# Revit family: Accessory-Teknion-EMWW_Thought_Board_Magnetic_Wood-R2016
name_source: partatom
category: Furniture
revit_build: Autodesk Revit 2018 (Build: 20190510_1515(x64)
units: mm (PartAtom-declared; Revit-internal decimal feet)

## family parameters
Always vertical = Yes
Cut with Voids When Loaded = No
OmniClass Number = 23.40.20.00
OmniClass Title = General Furniture and Specialties
Room Calculation Point = No
Shared = Yes
Work Plane-Based = No

## types (1)
- Thought Board, Magnetic Wood
    Assembly Code = E2020200
    Description = Thought Board, Magnetic Wood
    Manufacturer = Teknion
    Manufacturer Fax = 416.661.4586
    Model = EMWW__
    Part Number = EMWW
    Product Documentation Link = https://assets.teknion.com
    Product Line = Emote
    Product Page URL = https://www.teknion.com
    Series = Emote
    Sustainability Data = https://www.teknion.com
    URL = www.teknion.com
    Unit Weight URL = http://www.teknion.com
    Warranty = http://www.teknion.com

## geometry (parser evidence)
native form markers: Blend x31, Sweep x3
no freeform markers — native parametric forms only
